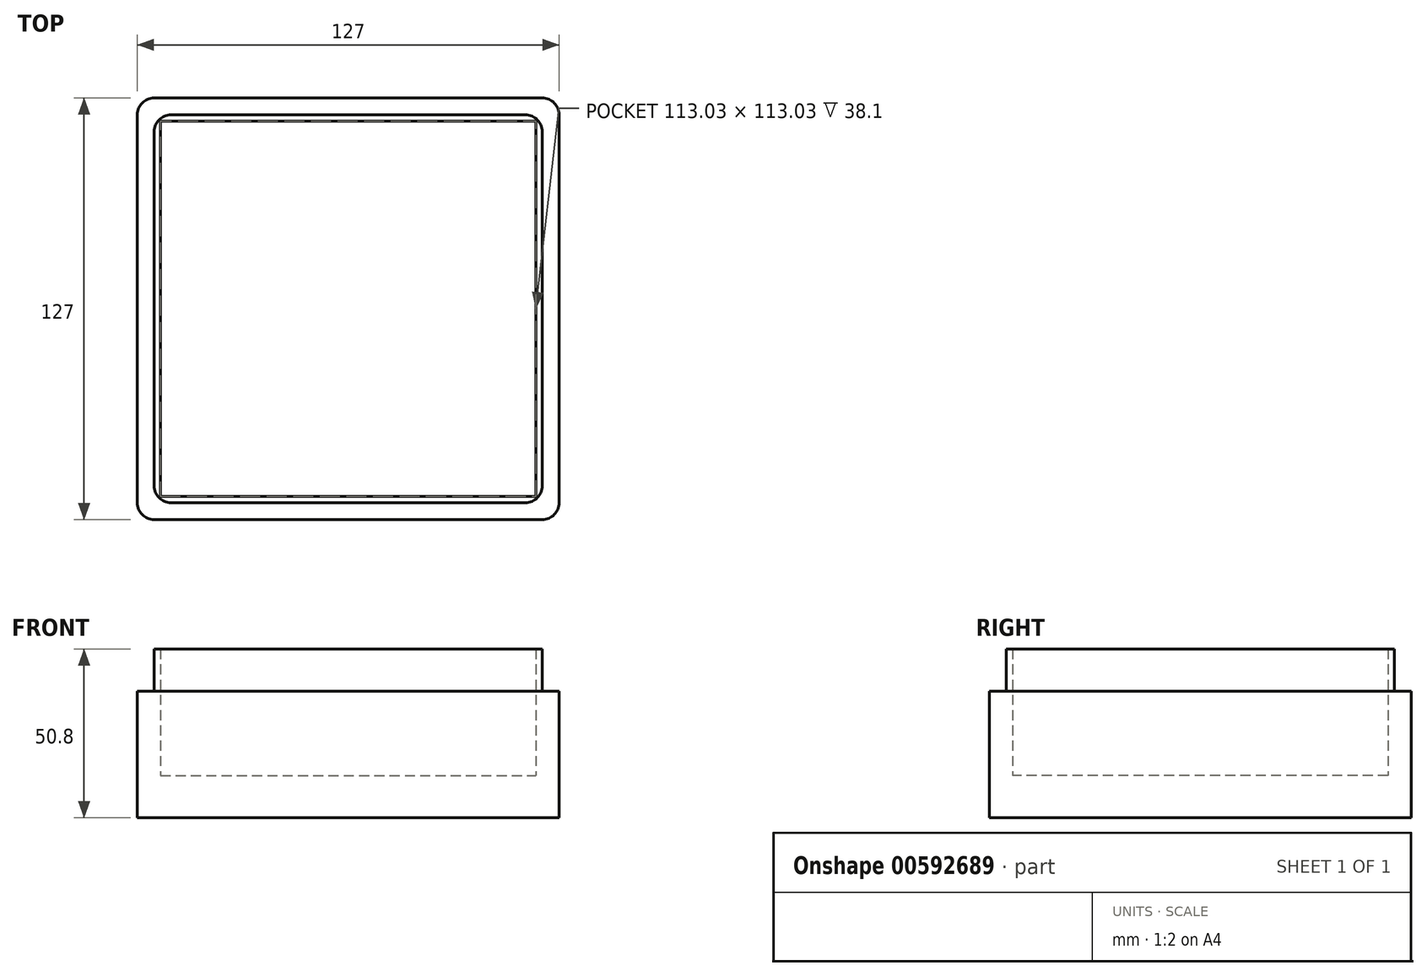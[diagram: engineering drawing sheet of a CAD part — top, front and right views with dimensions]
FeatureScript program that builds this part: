
annotation { "Feature Type Name" : "Feature", "Feature Type Description" : "" }
export const myFeature = defineFeature(function(context is Context, id is Id, definition is map)
    precondition{}
    {
        {
            var Q0;
            Q0=qCreatedBy(makeId("Top.planeOp"),FACE);
            var sketch = newSketch(context, id + "F0", { "sketchPlane" : qUnion([Q0])});
            skLineSegment(sketch, "E0.bottom", {"start": v(-56.52, 56.52) * mm, "end": v(56.52, 56.52) * mm});
            skLineSegment(sketch, "E0.top", {"start": v(-56.52, -56.52) * mm, "end": v(56.52, -56.52) * mm});
            skLineSegment(sketch, "E0.left", {"start": v(-56.52, 56.52) * mm, "end": v(-56.52, -56.52) * mm});
            skLineSegment(sketch, "E0.right", {"start": v(56.52, 56.52) * mm, "end": v(56.52, -56.52) * mm});
            skLineSegment(sketch, "E1.bottom", {"start": v(63.5, -63.5) * mm, "end": v(-63.5, -63.5) * mm});
            skLineSegment(sketch, "E1.top", {"start": v(63.5, 63.5) * mm, "end": v(-63.5, 63.5) * mm});
            skLineSegment(sketch, "E1.left", {"start": v(63.5, -63.5) * mm, "end": v(63.5, 63.5) * mm});
            skLineSegment(sketch, "E1.right", {"start": v(-63.5, -63.5) * mm, "end": v(-63.5, 63.5) * mm});
            skPoint(sketch, "E1.middle", {"position": v(0, 0) * mm});
            skSolve(sketch);
        }
        {
            var Q0;
            Q0 = qSketchRegion(id + "F0", true);
            extrude(context, id + "F1", {"entities" : qUnion([Q0]), "depth" : 38.1 * mm, "offsetDistance" : 25.4 * mm});
        }
        {
            var Q0;
            Q0=qCreatedBy(makeId("Top.planeOp"),FACE);
            var sketch = newSketch(context, id + "F2", { "sketchPlane" : qUnion([Q0])});
            skLineSegment(sketch, "E2.bottom", {"start": v(-56.52, 56.52) * mm, "end": v(56.52, 56.52) * mm});
            skLineSegment(sketch, "E2.top", {"start": v(-56.52, -56.52) * mm, "end": v(56.52, -56.52) * mm});
            skLineSegment(sketch, "E2.left", {"start": v(-56.52, 56.52) * mm, "end": v(-56.52, -56.52) * mm});
            skLineSegment(sketch, "E2.right", {"start": v(56.52, 56.52) * mm, "end": v(56.52, -56.52) * mm});
            skPoint(sketch, "E2.middle", {"position": v(0, 0) * mm});
            skSolve(sketch);
        }
        {
            var Q0;
            Q0=makeQuery(id+"F2.imprint","IMPRINT",FACE,{"disambiguationData":[TD([[makeQuery(id+"F2.imprint","IMPRINT",EDGE,{"derivedFrom":sQuery(id+"F2.wireOp",EDGE,"E2.bottom")}),-1.0]])]});
            extrude(context, id + "F3", {"entities" : qUnion([Q0]), "operationType" : NewBodyOperationType.ADD, "depth" : 12.7 * mm, "offsetDistance" : 25.4 * mm});
        }
        {
            var Q0;
            Q0=makeQuery(id+"F1.opExtrude","SWEPT_EDGE",EDGE,{"disambiguationData":[OSD([sQuery(id+"F0.wireOp",EDGE,"E1.bottom"),sQuery(id+"F0.wireOp",EDGE,"E1.right")])]});
            var Q1;
            Q1=makeQuery(id+"F1.opExtrude","SWEPT_EDGE",EDGE,{"disambiguationData":[OSD([sQuery(id+"F0.wireOp",EDGE,"E1.top"),sQuery(id+"F0.wireOp",EDGE,"E1.right")])]});
            var Q2;
            Q2=makeQuery(id+"F1.opExtrude","SWEPT_EDGE",EDGE,{"disambiguationData":[OSD([sQuery(id+"F0.wireOp",EDGE,"E1.top"),sQuery(id+"F0.wireOp",EDGE,"E1.left")])]});
            var Q3;
            Q3=makeQuery(id+"F1.opExtrude","SWEPT_EDGE",EDGE,{"disambiguationData":[OSD([sQuery(id+"F0.wireOp",EDGE,"E1.bottom"),sQuery(id+"F0.wireOp",EDGE,"E1.left")])]});
            fillet(context, id + "F4", {"entities" : qUnion([Q0, Q1, Q2, Q3]), "radius" : 5.08 * mm, "tangentPropagation" : true, "allowEdgeOverflow" : false});
        }
        {
            var Q0;
            Q0=makeQuery(id+"F1.opExtrude","CAP_FACE",FACE,{"disambiguationData":[OSD([sQuery(id+"F0.wireOp",EDGE,"E0.bottom"),sQuery(id+"F0.wireOp",EDGE,"E0.top"),sQuery(id+"F0.wireOp",EDGE,"E0.left"),sQuery(id+"F0.wireOp",EDGE,"E0.right"),sQuery(id+"F0.wireOp",EDGE,"E1.bottom"),sQuery(id+"F0.wireOp",EDGE,"E1.top"),sQuery(id+"F0.wireOp",EDGE,"E1.left"),sQuery(id+"F0.wireOp",EDGE,"E1.right")])],"isStart":false});
            var sketch = newSketch(context, id + "F5", { "sketchPlane" : qUnion([Q0])});
            skLineSegment(sketch, "E3.bottom", {"start": v(-58.42, 58.42) * mm, "end": v(58.42, 58.42) * mm});
            skLineSegment(sketch, "E3.top", {"start": v(-58.42, -58.42) * mm, "end": v(58.42, -58.42) * mm});
            skLineSegment(sketch, "E3.left", {"start": v(-58.42, 58.42) * mm, "end": v(-58.42, -58.42) * mm});
            skLineSegment(sketch, "E3.right", {"start": v(58.42, 58.42) * mm, "end": v(58.42, -58.42) * mm});
            skPoint(sketch, "E3.middle", {"position": v(0, 0) * mm});
            skSolve(sketch);
        }
        {
            var Q0;
            Q0=makeQuery(id+"F5.imprint","IMPRINT",FACE,{"disambiguationData":[TD([[makeQuery(id+"F5.imprint","IMPRINT",EDGE,{"derivedFrom":sQuery(id+"F5.wireOp",EDGE,"E3.bottom")}),-1.0]])]});
            extrude(context, id + "F6", {"entities" : qUnion([Q0]), "operationType" : NewBodyOperationType.ADD, "depth" : 12.7 * mm, "offsetDistance" : 25.4 * mm});
        }
        {
            var Q0;
            Q0=makeQuery(id+"F6.opExtrude","SWEPT_EDGE",EDGE,{"disambiguationData":[OSD([sQuery(id+"F5.wireOp",EDGE,"E3.top"),sQuery(id+"F5.wireOp",EDGE,"E3.left")])]});
            var Q1;
            Q1=makeQuery(id+"F6.opExtrude","SWEPT_EDGE",EDGE,{"disambiguationData":[OSD([sQuery(id+"F5.wireOp",EDGE,"E3.top"),sQuery(id+"F5.wireOp",EDGE,"E3.right")])]});
            var Q2;
            Q2=makeQuery(id+"F6.opExtrude","SWEPT_EDGE",EDGE,{"disambiguationData":[OSD([sQuery(id+"F5.wireOp",EDGE,"E3.bottom"),sQuery(id+"F5.wireOp",EDGE,"E3.right")])]});
            var Q3;
            Q3=makeQuery(id+"F6.opExtrude","SWEPT_EDGE",EDGE,{"disambiguationData":[OSD([sQuery(id+"F5.wireOp",EDGE,"E3.bottom"),sQuery(id+"F5.wireOp",EDGE,"E3.left")])]});
            fillet(context, id + "F7", {"entities" : qUnion([Q0, Q1, Q2, Q3]), "radius" : 5.08 * mm, "tangentPropagation" : true, "allowEdgeOverflow" : false});
        }
    });
